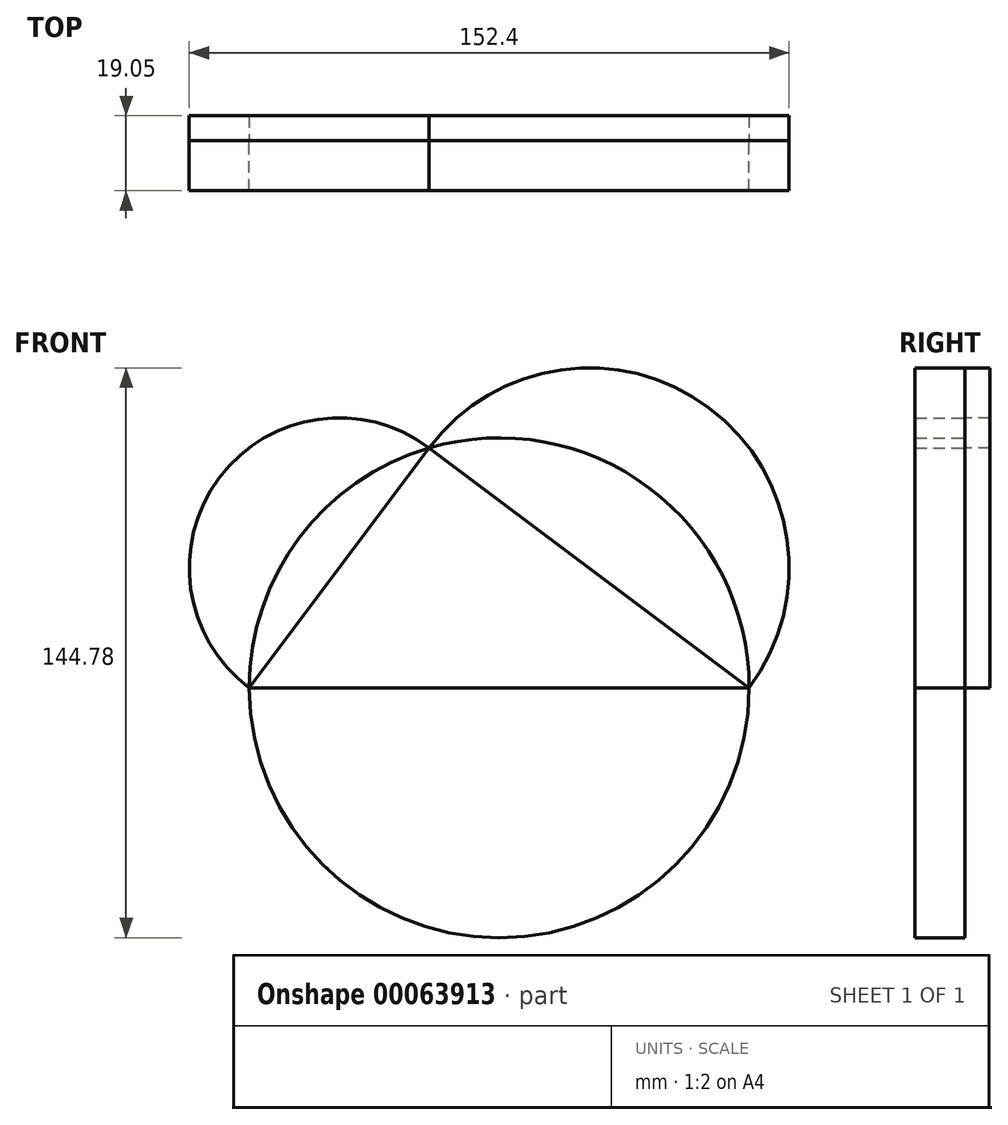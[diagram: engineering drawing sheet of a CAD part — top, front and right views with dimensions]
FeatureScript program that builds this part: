
annotation { "Feature Type Name" : "Feature", "Feature Type Description" : "" }
export const myFeature = defineFeature(function(context is Context, id is Id, definition is map)
    precondition{}
    {
        {
            var Q0;
            Q0=qCreatedBy(makeId("Front.planeOp"),FACE);
            var sketch = newSketch(context, id + "F0", { "sketchPlane" : qUnion([Q0])});
            skCircle(sketch, "E0", {"center": v(0, 0) * mm, "radius": 63.5 * mm});
            skLineSegment(sketch, "E1", {"start": v(-17.78, 60.96) * mm, "end": v(-63.5, 0) * mm});
            skLineSegment(sketch, "E2", {"start": v(-63.5, 0) * mm, "end": v(63.5, 0) * mm});
            skLineSegment(sketch, "E3", {"start": v(63.5, 0) * mm, "end": v(-17.78, 60.96) * mm});
            skArc(sketch, "E4", {"start": v(-17.78, 60.96) * mm, "mid": v(-71.12, 53.34) * mm, "end": v(-63.5, 0) * mm});
            skArc(sketch, "E5", {"start": v(63.5, 0) * mm, "mid": v(53.34, 71.12) * mm, "end": v(-17.78, 60.96) * mm});
            skSolve(sketch);
        }
        {
            var Q0;
            Q0=makeQuery(id+"F0.imprint","IMPRINT",FACE,{"disambiguationData":[TD([[makeQuery(id+"F0.imprint","IMPRINT",EDGE,{"derivedFrom":sQuery(id+"F0.wireOp",EDGE,"E1")}),1.0]])]});
            var Q1;
            {var subQ0=sQuery(id+"F0.wireOp",EDGE,"E5");Q1=makeQuery(id+"F0.imprint","IMPRINT",FACE,{"disambiguationData":[TD([[makeQuery(id+"F0.imprint","IMPRINT",EDGE,{"derivedFrom":subQ0}),1.0]])]});}
            var Q2;
            {var subQ0=sQuery(id+"F0.wireOp",EDGE,"E4");Q2=makeQuery(id+"F0.imprint","IMPRINT",FACE,{"disambiguationData":[TD([[makeQuery(id+"F0.imprint","IMPRINT",EDGE,{"derivedFrom":subQ0}),1.0]])]});}
            extrude(context, id + "F1", {"entities" : qUnion([Q0, Q1, Q2]), "depth" : 12.7 * mm});
        }
        {
            var Q0;
            {var subQ0=sQuery(id+"F0.wireOp",EDGE,"E2");Q0=makeQuery(id+"F0.imprint","IMPRINT",FACE,{"disambiguationData":[TD([[makeQuery(id+"F0.imprint","IMPRINT",EDGE,{"derivedFrom":subQ0}),-1.0]])]});}
            var Q1;
            {var subQ1=sQuery(id+"F0.wireOp",EDGE,"E3");Q1=makeQuery(id+"F0.imprint","IMPRINT",FACE,{"disambiguationData":[TD([[makeQuery(id+"F0.imprint","IMPRINT",EDGE,{"derivedFrom":subQ1}),-1.0]])]});}
            var Q2;
            {var subQ1=sQuery(id+"F0.wireOp",EDGE,"E1");Q2=makeQuery(id+"F0.imprint","IMPRINT",FACE,{"disambiguationData":[TD([[makeQuery(id+"F0.imprint","IMPRINT",EDGE,{"derivedFrom":subQ1}),-1.0]])]});}
            extrude(context, id + "F2", {"entities" : qUnion([Q0, Q1, Q2]), "depth" : 12.7 * mm});
        }
        {
            var Q0;
            {var subQ1=sQuery(id+"F0.wireOp",EDGE,"E1");Q0=makeQuery(id+"F0.imprint","IMPRINT",FACE,{"disambiguationData":[TD([[makeQuery(id+"F0.imprint","IMPRINT",EDGE,{"derivedFrom":subQ1}),-1.0]])]});}
            var Q1;
            {var subQ0=sQuery(id+"F0.wireOp",EDGE,"E4");Q1=makeQuery(id+"F0.imprint","IMPRINT",FACE,{"disambiguationData":[TD([[makeQuery(id+"F0.imprint","IMPRINT",EDGE,{"derivedFrom":subQ0}),1.0]])]});}
            var Q2;
            {var subQ1=sQuery(id+"F0.wireOp",EDGE,"E3");Q2=makeQuery(id+"F0.imprint","IMPRINT",FACE,{"disambiguationData":[TD([[makeQuery(id+"F0.imprint","IMPRINT",EDGE,{"derivedFrom":subQ1}),-1.0]])]});}
            var Q3;
            {var subQ0=sQuery(id+"F0.wireOp",EDGE,"E5");Q3=makeQuery(id+"F0.imprint","IMPRINT",FACE,{"disambiguationData":[TD([[makeQuery(id+"F0.imprint","IMPRINT",EDGE,{"derivedFrom":subQ0}),1.0]])]});}
            extrude(context, id + "F3", {"entities" : qUnion([Q0, Q1, Q2, Q3]), "oppositeDirection" : true, "depth" : 6.35 * mm});
        }
    });
